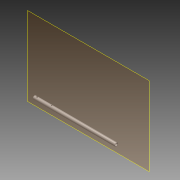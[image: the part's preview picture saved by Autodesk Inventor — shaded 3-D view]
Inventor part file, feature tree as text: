
AUTODESK INVENTOR PART (.ipt)
format: ipt  version: 2014 SP1 (Build 180222100, 222)  size: 128,512 bytes
history: native  units: in
note: dims shown in document units (in); Inventor stores cm internally (conversion verified against a paired STEP export)
features: sketch x4, plane x2, extrude x2, sweep x1
ambient origin geometry x8: Origin, YZ Plane, XZ Plane, XY Plane, X Axis, Y Axis, Z Axis, Center Point
bodies: Solid1 (feature_tree)
feature tree (9):
  sweep  "Sweep1"
  plane  "Work Plane1"
  extrude  "Extrusion1"  Depth=4.0in
  plane  "Work Plane2"
  extrude  "Extrusion2"  Depth=0.5in
  sketch  "Sketch1"  dims[d0=12.0in d1=4.0in]
  sketch  "Sketch2"  dims[d2=2.0in d3=4.0in]
  sketch  "Sketch3"  dims[d4=4.0in d5=0.5in]
  sketch  "Sketch4"  dims[d6=0.0in d7=25.0in d8=0.375in d9=0.164in d10=2.5in d11=0.25in d12=1.0in d13=0.0in d14=0.194in d15=0.375in d16=0.25in d17=12.0in d18=1.0in d19=0.0in]
